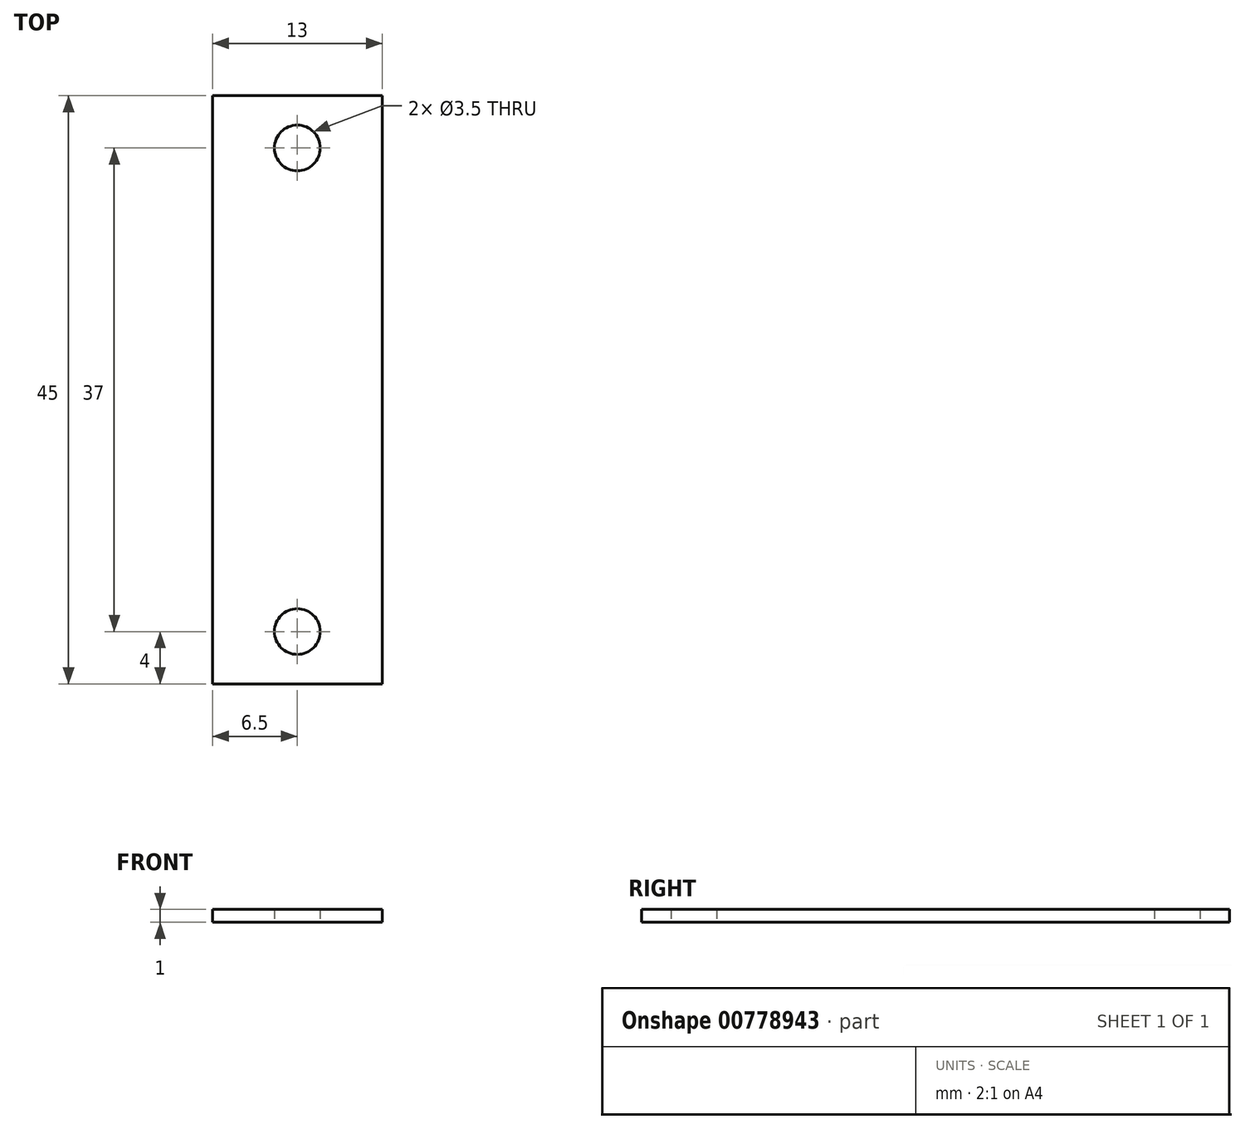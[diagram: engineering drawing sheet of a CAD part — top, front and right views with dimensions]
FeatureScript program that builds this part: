
annotation { "Feature Type Name" : "Feature", "Feature Type Description" : "" }
export const myFeature = defineFeature(function(context is Context, id is Id, definition is map)
    precondition{}
    {
        {
            var Q0;
            Q0=qCreatedBy(makeId("Top.planeOp"),FACE);
            var sketch = newSketch(context, id + "F0", { "sketchPlane" : qUnion([Q0])});
            skLineSegment(sketch, "E0.bottom", {"start": v(6.5, -22.5) * mm, "end": v(-6.5, -22.5) * mm});
            skLineSegment(sketch, "E0.top", {"start": v(6.5, 22.5) * mm, "end": v(-6.5, 22.5) * mm});
            skLineSegment(sketch, "E0.left", {"start": v(6.5, -22.5) * mm, "end": v(6.5, 22.5) * mm});
            skLineSegment(sketch, "E0.right", {"start": v(-6.5, -22.5) * mm, "end": v(-6.5, 22.5) * mm});
            skPoint(sketch, "E0.middle", {"position": v(0, 0) * mm});
            skCircle(sketch, "E1", {"center": v(0, -18.5) * mm, "radius": 1.75 * mm});
            skCircle(sketch, "E2", {"center": v(0, 18.5) * mm, "radius": 1.75 * mm});
            skSolve(sketch);
        }
        {
            var Q0;
            Q0 = qSketchRegion(id + "F0", true);
            extrude(context, id + "F1", {"entities" : qUnion([Q0]), "depth" : 1 * mm, "offsetDistance" : 25.4 * mm});
        }
    });
